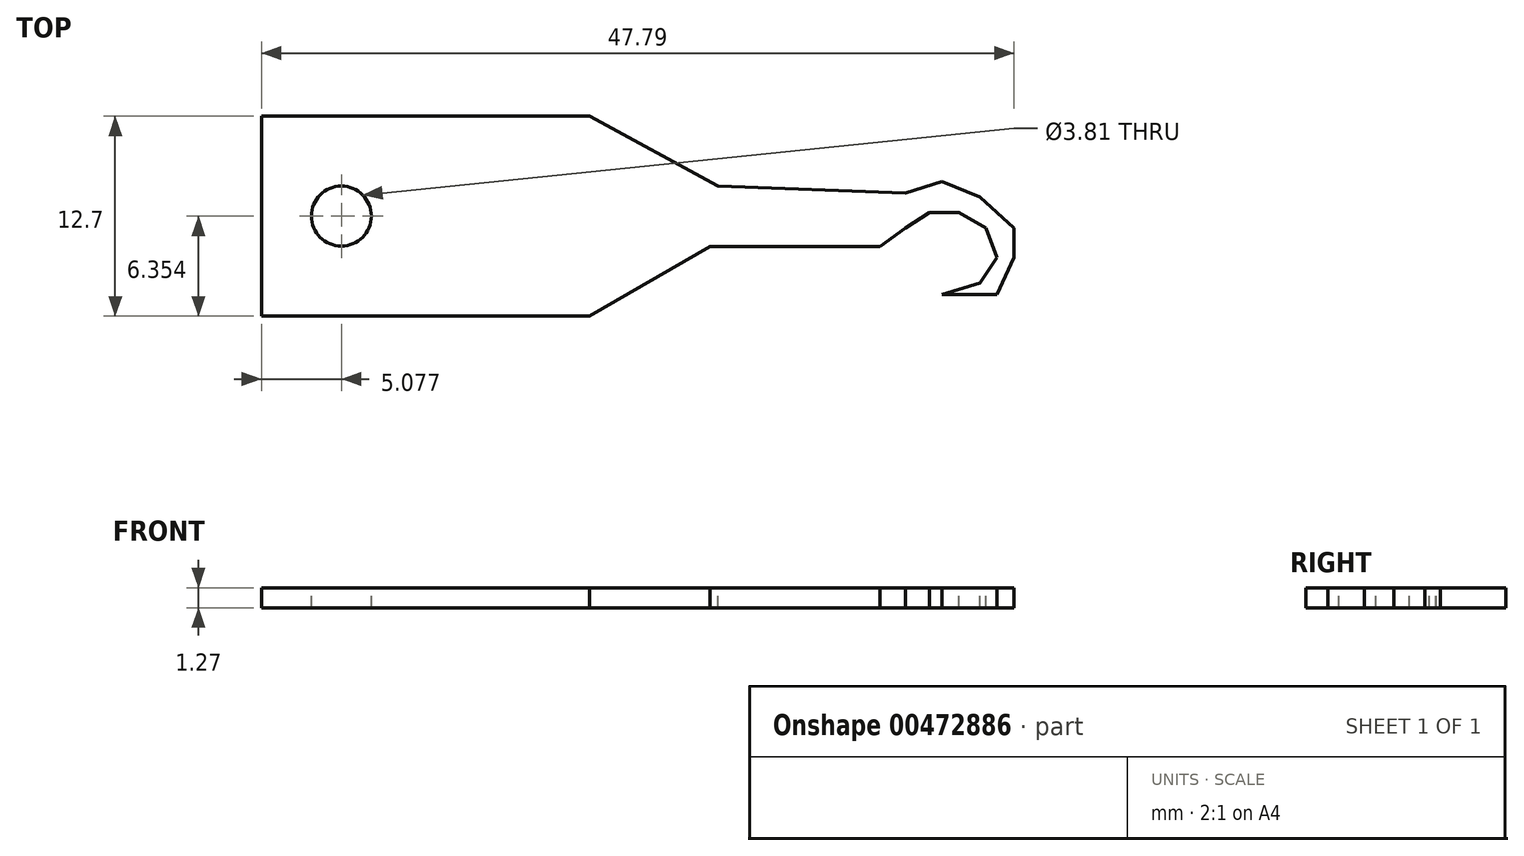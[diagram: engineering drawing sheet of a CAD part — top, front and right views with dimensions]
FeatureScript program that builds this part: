
annotation { "Feature Type Name" : "Feature", "Feature Type Description" : "" }
export const myFeature = defineFeature(function(context is Context, id is Id, definition is map)
    precondition{}
    {
        {
            var Q0;
            Q0=qCreatedBy(makeId("Top.planeOp"),FACE);
            var sketch = newSketch(context, id + "F0", { "sketchPlane" : qUnion([Q0])});
            skLineSegment(sketch, "E0.bottom", {"start": v(18.06, -27.4) * mm, "end": v(68.86, -27.4) * mm});
            skLineSegment(sketch, "E0.top", {"start": v(18.06, -14.7) * mm, "end": v(68.86, -14.7) * mm});
            skLineSegment(sketch, "E0.left", {"start": v(18.06, -27.4) * mm, "end": v(18.06, -14.7) * mm});
            skLineSegment(sketch, "E0.right", {"start": v(68.86, -27.4) * mm, "end": v(68.86, -14.7) * mm});
            skSolve(sketch);
        }
        {
            var Q0;
            Q0=makeQuery(id+"F0.imprint","IMPRINT",FACE,{"disambiguationData":[TD([[makeQuery(id+"F0.imprint","IMPRINT",EDGE,{"derivedFrom":sQuery(id+"F0.wireOp",EDGE,"E0.bottom")}),1.0]])]});
            extrude(context, id + "F1", {"entities" : qUnion([Q0]), "depth" : 1.27 * mm});
        }
        {
            var Q0;
            Q0=makeQuery(id+"F1.opExtrude","CAP_FACE",FACE,{"disambiguationData":[OSD([sQuery(id+"F0.wireOp",EDGE,"E0.bottom"),sQuery(id+"F0.wireOp",EDGE,"E0.top"),sQuery(id+"F0.wireOp",EDGE,"E0.left"),sQuery(id+"F0.wireOp",EDGE,"E0.right")])],"isStart":false});
            var sketch = newSketch(context, id + "F2", { "sketchPlane" : qUnion([Q0])});
            skCircle(sketch, "E1", {"center": v(23.14, -21.06) * mm, "radius": 1.9 * mm});
            skSolve(sketch);
        }
        {
            var Q0;
            Q0=makeQuery(id+"F2.imprint","IMPRINT",FACE,{"disambiguationData":[TD([[makeQuery(id+"F2.imprint","IMPRINT",EDGE,{"derivedFrom":sQuery(id+"F2.wireOp",EDGE,"E1")}),1.0]])]});
            extrude(context, id + "F3", {"entities" : qUnion([Q0]), "operationType" : NewBodyOperationType.REMOVE, "oppositeDirection" : true, "depth" : 25.4 * mm});
        }
        {
            var Q0;
            Q0=makeQuery(id+"F1.opExtrude","CAP_FACE",FACE,{"disambiguationData":[OSD([sQuery(id+"F0.wireOp",EDGE,"E0.bottom"),sQuery(id+"F0.wireOp",EDGE,"E0.top"),sQuery(id+"F0.wireOp",EDGE,"E0.left"),sQuery(id+"F0.wireOp",EDGE,"E0.right")])],"isStart":false});
            var sketch = newSketch(context, id + "F4", { "sketchPlane" : qUnion([Q0])});
            skLineSegment(sketch, "E2", {"start": v(57.36, -22.98) * mm, "end": v(46.55, -22.98) * mm});
            skLineSegment(sketch, "E3", {"start": v(46.55, -22.98) * mm, "end": v(38.9, -27.4) * mm});
            skPoint(sketch, "E4", {"position": v(68.86, -21.06) * mm});
            skLineSegment(sketch, "E5", {"start": v(47.07, -19.14) * mm, "end": v(38.9, -14.7) * mm});
            skLineSegment(sketch, "E6", {"start": v(57.36, -22.98) * mm, "end": v(58.97, -21.82) * mm});
            skLineSegment(sketch, "E7", {"start": v(58.97, -21.82) * mm, "end": v(60.49, -20.84) * mm});
            skLineSegment(sketch, "E8", {"start": v(60.49, -20.84) * mm, "end": v(62.37, -20.84) * mm});
            skLineSegment(sketch, "E9", {"start": v(62.37, -20.84) * mm, "end": v(64.06, -21.82) * mm});
            skLineSegment(sketch, "E10", {"start": v(64.06, -21.82) * mm, "end": v(64.78, -23.7) * mm});
            skLineSegment(sketch, "E11", {"start": v(64.78, -23.7) * mm, "end": v(63.7, -25.3) * mm});
            skLineSegment(sketch, "E12", {"start": v(63.7, -25.3) * mm, "end": v(61.3, -26.02) * mm});
            skLineSegment(sketch, "E13", {"start": v(61.3, -26.02) * mm, "end": v(64.78, -26.02) * mm});
            skLineSegment(sketch, "E14", {"start": v(64.78, -26.02) * mm, "end": v(65.85, -23.7) * mm});
            skLineSegment(sketch, "E15", {"start": v(65.85, -23.7) * mm, "end": v(65.85, -21.82) * mm});
            skLineSegment(sketch, "E16", {"start": v(65.85, -21.82) * mm, "end": v(63.7, -19.85) * mm});
            skLineSegment(sketch, "E17", {"start": v(63.7, -19.85) * mm, "end": v(61.3, -18.87) * mm});
            skLineSegment(sketch, "E18", {"start": v(61.3, -18.87) * mm, "end": v(58.97, -19.58) * mm});
            skLineSegment(sketch, "E19", {"start": v(58.97, -19.58) * mm, "end": v(47.07, -19.14) * mm});
            skSolve(sketch);
        }
        {
            var Q0;
            Q0=makeQuery(id+"F4.imprint","IMPRINT",FACE,{"disambiguationData":[TD([[makeQuery(id+"F4.imprint","IMPRINT",EDGE,{"derivedFrom":sQuery(id+"F4.wireOp",EDGE,"E2")}),1.0]])]});
            extrude(context, id + "F5", {"entities" : qUnion([Q0]), "operationType" : NewBodyOperationType.REMOVE, "oppositeDirection" : true, "depth" : 25.4 * mm});
        }
    });
